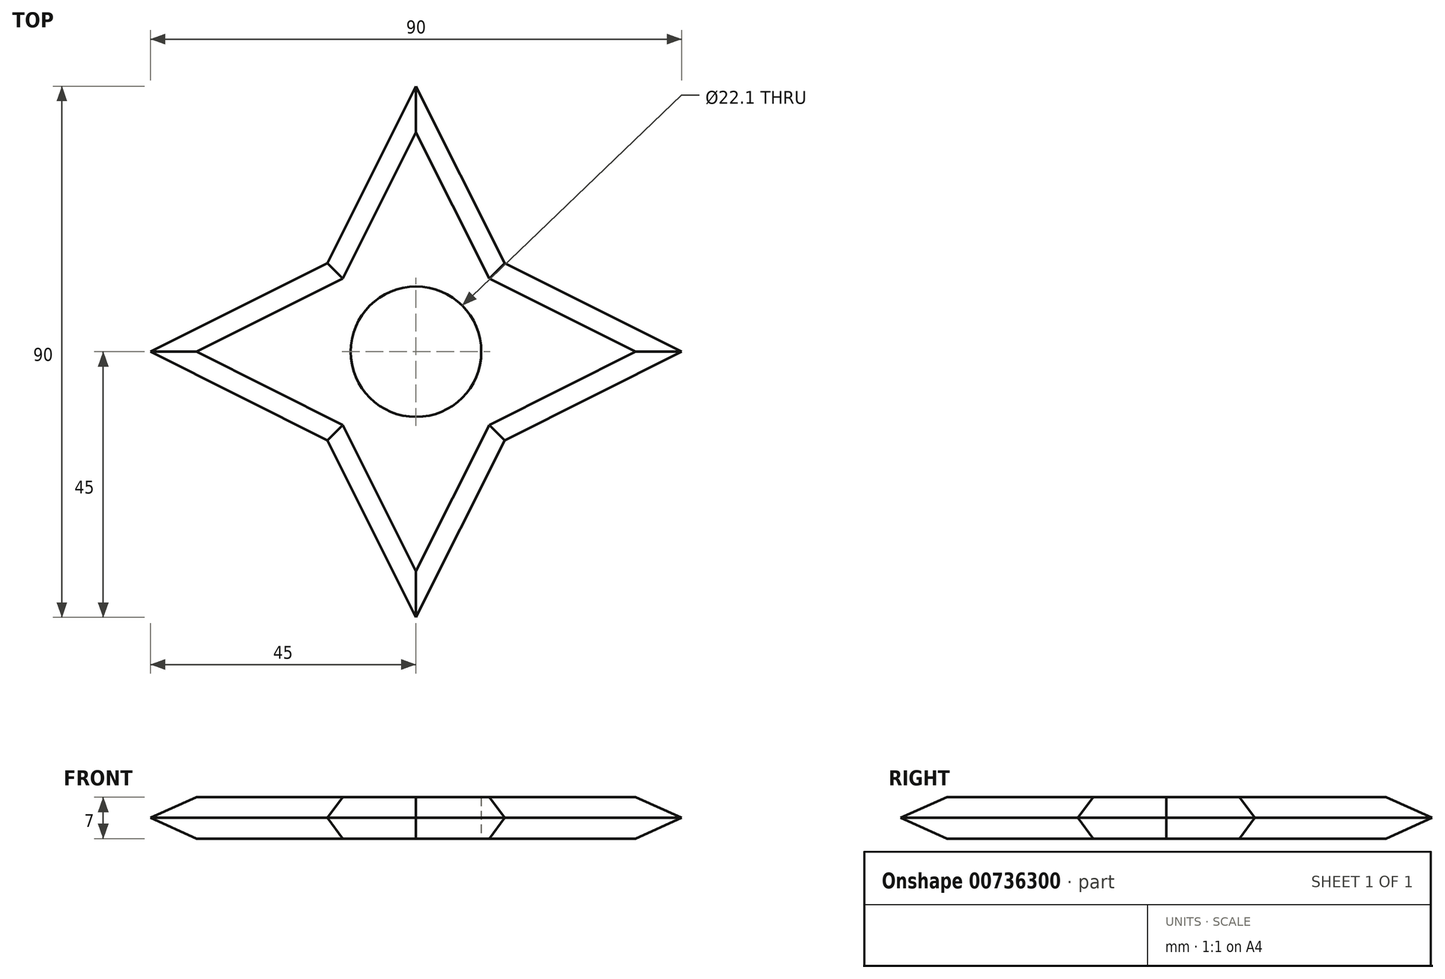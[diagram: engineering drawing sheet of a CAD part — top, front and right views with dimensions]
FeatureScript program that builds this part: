
annotation { "Feature Type Name" : "Feature", "Feature Type Description" : "" }
export const myFeature = defineFeature(function(context is Context, id is Id, definition is map)
    precondition{}
    {
        {
            var Q0;
            Q0=qCreatedBy(makeId("Top.planeOp"),FACE);
            var sketch = newSketch(context, id + "F0", { "sketchPlane" : qUnion([Q0])});
            skLineSegment(sketch, "E0.bottom", {"start": v(-15, 15) * mm, "end": v(15, 15) * mm});
            skLineSegment(sketch, "E0.top", {"start": v(-15, -15) * mm, "end": v(15, -15) * mm});
            skLineSegment(sketch, "E0.left", {"start": v(-15, 15) * mm, "end": v(-15, -15) * mm});
            skLineSegment(sketch, "E0.right", {"start": v(15, 15) * mm, "end": v(15, -15) * mm});
            skPoint(sketch, "E0.middle", {"position": v(0, 0) * mm});
            skCircle(sketch, "E1", {"center": v(0, 0) * mm, "radius": 11.05 * mm});
            skLineSegment(sketch, "E2", {"start": v(0, 15) * mm, "end": v(0, 45) * mm});
            skLineSegment(sketch, "E3", {"start": v(15, 0) * mm, "end": v(45, 0) * mm});
            skLineSegment(sketch, "E4", {"start": v(0, -15) * mm, "end": v(0, -45) * mm});
            skLineSegment(sketch, "E5", {"start": v(-15, 0) * mm, "end": v(-45, 0) * mm});
            skLineSegment(sketch, "E6", {"start": v(0, 45) * mm, "end": v(-15, 15) * mm});
            skLineSegment(sketch, "E7", {"start": v(0, 45) * mm, "end": v(15, 15) * mm});
            skLineSegment(sketch, "E8", {"start": v(15, 15) * mm, "end": v(45, 0) * mm});
            skLineSegment(sketch, "E9", {"start": v(45, 0) * mm, "end": v(15, -15) * mm});
            skLineSegment(sketch, "E10", {"start": v(0, -45) * mm, "end": v(15, -15) * mm});
            skLineSegment(sketch, "E11", {"start": v(-15, -15) * mm, "end": v(0, -45) * mm});
            skLineSegment(sketch, "E12", {"start": v(-15, 15) * mm, "end": v(-45, 0) * mm});
            skLineSegment(sketch, "E13", {"start": v(-45, 0) * mm, "end": v(-15, -15) * mm});
            skSolve(sketch);
        }
        {
            var Q0;
            {var subQ2=sQuery(id+"F0.wireOp",EDGE,"E2");Q0=makeQuery(id+"F0.imprint","IMPRINT",FACE,{"disambiguationData":[TD([[makeQuery(id+"F0.imprint","IMPRINT",EDGE,{"derivedFrom":subQ2}),1.0]])]});}
            var Q1;
            {var subQ2=sQuery(id+"F0.wireOp",EDGE,"E2");Q1=makeQuery(id+"F0.imprint","IMPRINT",FACE,{"disambiguationData":[TD([[makeQuery(id+"F0.imprint","IMPRINT",EDGE,{"derivedFrom":subQ2}),-1.0]])]});}
            var Q2;
            Q2=makeQuery(id+"F0.imprint","IMPRINT",FACE,{"disambiguationData":[TD([[makeQuery(id+"F0.imprint","IMPRINT",EDGE,{"derivedFrom":sQuery(id+"F0.wireOp",EDGE,"E1")}),-1.0]])]});
            var Q3;
            {var subQ2=sQuery(id+"F0.wireOp",EDGE,"E5");Q3=makeQuery(id+"F0.imprint","IMPRINT",FACE,{"disambiguationData":[TD([[makeQuery(id+"F0.imprint","IMPRINT",EDGE,{"derivedFrom":subQ2}),1.0]])]});}
            var Q4;
            {var subQ2=sQuery(id+"F0.wireOp",EDGE,"E5");Q4=makeQuery(id+"F0.imprint","IMPRINT",FACE,{"disambiguationData":[TD([[makeQuery(id+"F0.imprint","IMPRINT",EDGE,{"derivedFrom":subQ2}),-1.0]])]});}
            var Q5;
            {var subQ2=sQuery(id+"F0.wireOp",EDGE,"E4");Q5=makeQuery(id+"F0.imprint","IMPRINT",FACE,{"disambiguationData":[TD([[makeQuery(id+"F0.imprint","IMPRINT",EDGE,{"derivedFrom":subQ2}),-1.0]])]});}
            var Q6;
            {var subQ2=sQuery(id+"F0.wireOp",EDGE,"E4");Q6=makeQuery(id+"F0.imprint","IMPRINT",FACE,{"disambiguationData":[TD([[makeQuery(id+"F0.imprint","IMPRINT",EDGE,{"derivedFrom":subQ2}),1.0]])]});}
            var Q7;
            {var subQ2=sQuery(id+"F0.wireOp",EDGE,"E3");Q7=makeQuery(id+"F0.imprint","IMPRINT",FACE,{"disambiguationData":[TD([[makeQuery(id+"F0.imprint","IMPRINT",EDGE,{"derivedFrom":subQ2}),-1.0]])]});}
            var Q8;
            {var subQ2=sQuery(id+"F0.wireOp",EDGE,"E3");Q8=makeQuery(id+"F0.imprint","IMPRINT",FACE,{"disambiguationData":[TD([[makeQuery(id+"F0.imprint","IMPRINT",EDGE,{"derivedFrom":subQ2}),1.0]])]});}
            extrude(context, id + "F1", {"entities" : qUnion([Q0, Q1, Q2, Q3, Q4, Q5, Q6, Q7, Q8]), "depth" : 7 * mm, "offsetDistance" : 25 * mm});
        }
        {
            var Q0;
            Q0=makeQuery(id+"F1.opExtrude","CAP_EDGE",EDGE,{"disambiguationData":[OSD([sQuery(id+"F0.wireOp",EDGE,"E9")])],"isStart":false});
            var Q1;
            Q1=makeQuery(id+"F1.opExtrude","CAP_EDGE",EDGE,{"disambiguationData":[OSD([sQuery(id+"F0.wireOp",EDGE,"E10")])],"isStart":false});
            var Q2;
            Q2=makeQuery(id+"F1.opExtrude","CAP_EDGE",EDGE,{"disambiguationData":[OSD([sQuery(id+"F0.wireOp",EDGE,"E11")])],"isStart":false});
            var Q3;
            Q3=makeQuery(id+"F1.opExtrude","CAP_EDGE",EDGE,{"disambiguationData":[OSD([sQuery(id+"F0.wireOp",EDGE,"E13")])],"isStart":false});
            var Q4;
            Q4=makeQuery(id+"F1.opExtrude","CAP_EDGE",EDGE,{"disambiguationData":[OSD([sQuery(id+"F0.wireOp",EDGE,"E12")])],"isStart":false});
            var Q5;
            Q5=makeQuery(id+"F1.opExtrude","CAP_EDGE",EDGE,{"disambiguationData":[OSD([sQuery(id+"F0.wireOp",EDGE,"E6")])],"isStart":false});
            var Q6;
            Q6=makeQuery(id+"F1.opExtrude","CAP_EDGE",EDGE,{"disambiguationData":[OSD([sQuery(id+"F0.wireOp",EDGE,"E7")])],"isStart":false});
            var Q7;
            Q7=makeQuery(id+"F1.opExtrude","CAP_EDGE",EDGE,{"disambiguationData":[OSD([sQuery(id+"F0.wireOp",EDGE,"E8")])],"isStart":false});
            chamfer(context, id + "F2", {"entities" : qUnion([Q0, Q1, Q2, Q3, Q4, Q5, Q6, Q7]), "width" : 3.5 * mm, "tangentPropagation" : true});
        }
        {
            var Q0;
            Q0=makeQuery(id+"F1.opExtrude","CAP_EDGE",EDGE,{"disambiguationData":[OSD([sQuery(id+"F0.wireOp",EDGE,"E8")])],"isStart":true});
            var Q1;
            Q1=makeQuery(id+"F1.opExtrude","CAP_EDGE",EDGE,{"disambiguationData":[OSD([sQuery(id+"F0.wireOp",EDGE,"E7")])],"isStart":true});
            var Q2;
            Q2=makeQuery(id+"F1.opExtrude","CAP_EDGE",EDGE,{"disambiguationData":[OSD([sQuery(id+"F0.wireOp",EDGE,"E6")])],"isStart":true});
            var Q3;
            Q3=makeQuery(id+"F1.opExtrude","CAP_EDGE",EDGE,{"disambiguationData":[OSD([sQuery(id+"F0.wireOp",EDGE,"E12")])],"isStart":true});
            var Q4;
            Q4=makeQuery(id+"F1.opExtrude","CAP_EDGE",EDGE,{"disambiguationData":[OSD([sQuery(id+"F0.wireOp",EDGE,"E13")])],"isStart":true});
            var Q5;
            Q5=makeQuery(id+"F1.opExtrude","CAP_EDGE",EDGE,{"disambiguationData":[OSD([sQuery(id+"F0.wireOp",EDGE,"E11")])],"isStart":true});
            var Q6;
            Q6=makeQuery(id+"F1.opExtrude","CAP_EDGE",EDGE,{"disambiguationData":[OSD([sQuery(id+"F0.wireOp",EDGE,"E10")])],"isStart":true});
            var Q7;
            Q7=makeQuery(id+"F1.opExtrude","CAP_EDGE",EDGE,{"disambiguationData":[OSD([sQuery(id+"F0.wireOp",EDGE,"E9")])],"isStart":true});
            chamfer(context, id + "F3", {"entities" : qUnion([Q0, Q1, Q2, Q3, Q4, Q5, Q6, Q7]), "width" : 3.5 * mm, "tangentPropagation" : true});
        }
    });
